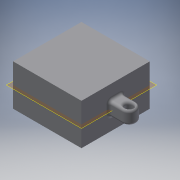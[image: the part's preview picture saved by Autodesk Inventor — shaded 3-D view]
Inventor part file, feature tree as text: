
AUTODESK INVENTOR PART (.ipt)
format: ipt  version: 2019 (Build 230136000, 136)  size: 153,088 bytes
history: native  units: mm
features: sketch x3, extrude x2, plane x1, hole x1, fillet x1
ambient origin geometry x8: Origin, YZ Plane, XZ Plane, XY Plane, X Axis, Y Axis, Z Axis, Center Point
bodies: Solid1 (feature_tree)
feature tree (8):
  extrude  "Extrusion1"  Depth=50.0mm
  plane  "Work Plane1"
  extrude  "Extrusion2"  Depth=10.0mm
  hole  "Hole1"  [1 undecoded]
  fillet  "Fillet1"  Radius=2.0mm
  sketch  "Sketch1"  dims[d0=50.0mm d1=50.0mm]
  sketch  "Sketch2"  dims[d2=30.0mm d3=0.0mm d4=10.0mm]
  sketch  "Sketch3"  dims[d5=10.0mm d6=10.0mm d7=0.0mm d8=5.5mm d9=6.0mm d10=10.4mm d11=2.0mm d12=90.0deg d13=8.0mm d14=20.594885mm d15=2.0mm]
note: 1 required parameter value undecoded (feature->parameter linkage not recoverable at this tier; creation-order binding heuristic only, values carry confidence <= 0.55)
